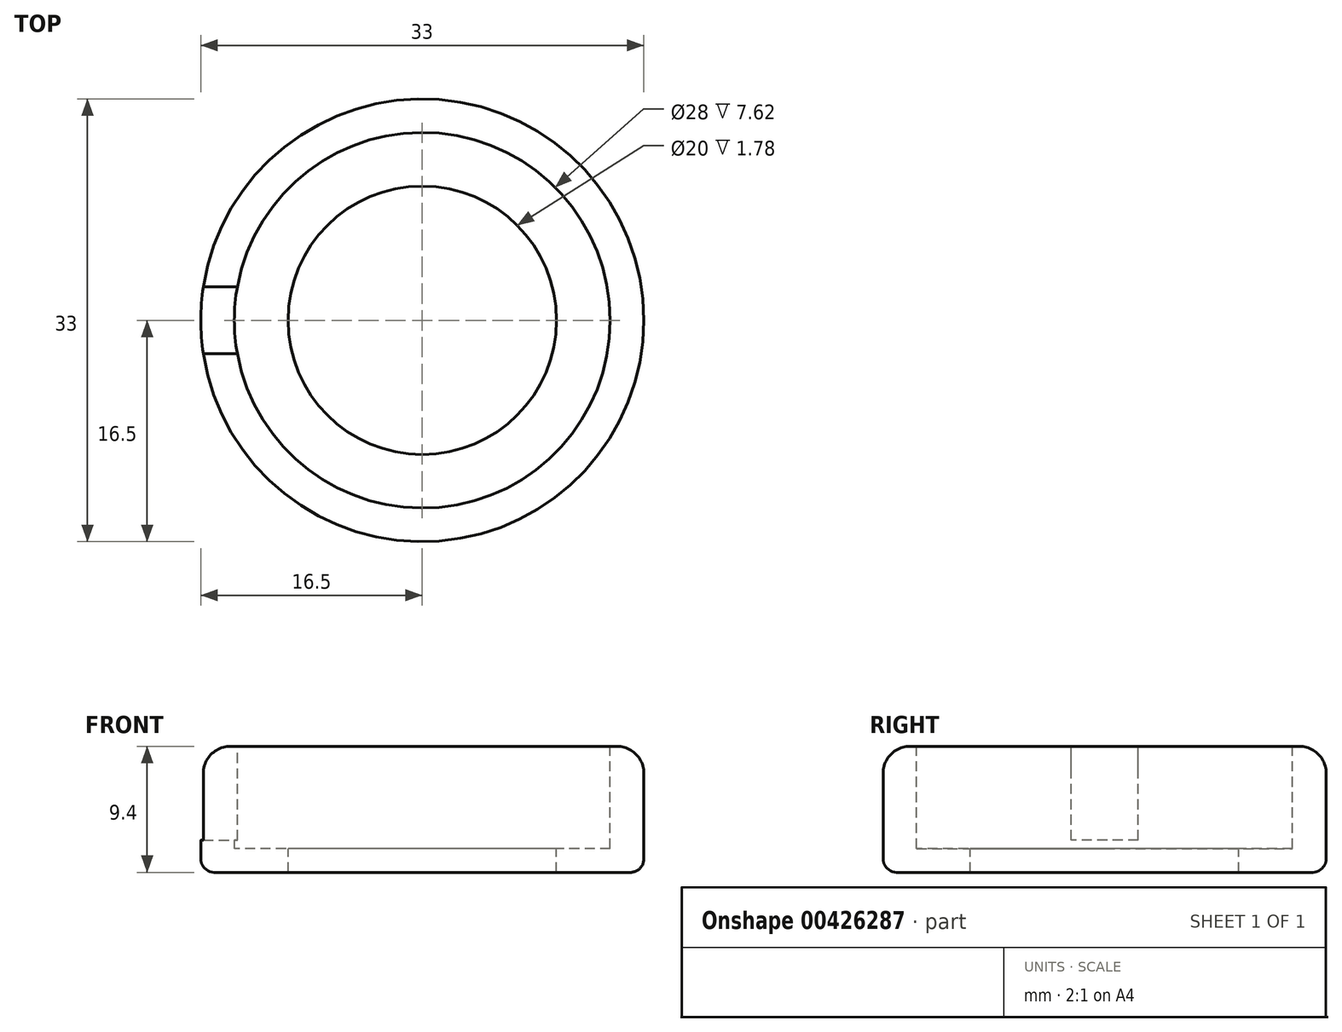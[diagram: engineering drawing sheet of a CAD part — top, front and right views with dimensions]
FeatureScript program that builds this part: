
annotation { "Feature Type Name" : "Feature", "Feature Type Description" : "" }
export const myFeature = defineFeature(function(context is Context, id is Id, definition is map)
    precondition{}
    {
        {
            var Q0;
            Q0=qCreatedBy(makeId("Top.planeOp"),FACE);
            var sketch = newSketch(context, id + "F0", { "sketchPlane" : qUnion([Q0])});
            skCircle(sketch, "E0", {"center": v(0, 0) * mm, "radius": 16.5 * mm});
            skSolve(sketch);
        }
        {
            var Q0;
            Q0 = qSketchRegion(id + "F0", true);
            extrude(context, id + "F1", {"entities" : qUnion([Q0]), "depth" : 9.4 * mm});
        }
        {
            var Q0;
            Q0=makeQuery(id+"F1.opExtrude","CAP_FACE",FACE,{"disambiguationData":[OSD([sQuery(id+"F0.wireOp",EDGE,"E0")])],"isStart":false});
            var sketch = newSketch(context, id + "F2", { "sketchPlane" : qUnion([Q0])});
            skCircle(sketch, "E1", {"center": v(0, 0) * mm, "radius": 14 * mm});
            skSolve(sketch);
        }
        {
            var Q0;
            Q0 = qSketchRegion(id + "F2", true);
            extrude(context, id + "F3", {"entities" : qUnion([Q0]), "operationType" : NewBodyOperationType.REMOVE, "oppositeDirection" : true, "depth" : 7.62 * mm});
        }
        {
            var Q0;
            Q0=makeQuery(id+"F1.opExtrude","CAP_EDGE",EDGE,{"disambiguationData":[OSD([sQuery(id+"F0.wireOp",EDGE,"E0")])],"isStart":false});
            fillet(context, id + "F4", {"entities" : qUnion([Q0]), "radius" : 2 * mm, "tangentPropagation" : true, "allowEdgeOverflow" : false});
        }
        {
            var Q0;
            Q0=makeQuery(id+"F1.opExtrude","CAP_FACE",FACE,{"disambiguationData":[OSD([sQuery(id+"F0.wireOp",EDGE,"E0")])],"isStart":false});
            var sketch = newSketch(context, id + "F5", { "sketchPlane" : qUnion([Q0])});
            skArc(sketch, "E2.0", {"start": v(-13.77, 2.5) * mm, "mid": v(-14, 0) * mm, "end": v(-13.77, -2.5) * mm});
            skArc(sketch, "E3.0", {"start": v(-16.3, 2.5) * mm, "mid": v(-16.5, 0) * mm, "end": v(-16.3, -2.5) * mm});
            skLineSegment(sketch, "E4", {"start": v(-14, 0) * mm, "end": v(-16.5, 0) * mm, "construction": true});
            skLineSegment(sketch, "E5", {"start": v(-16.3, 2.5) * mm, "end": v(-13.77, 2.5) * mm});
            skLineSegment(sketch, "E6.MirrorCS", {"start": v(-16.3, -2.5) * mm, "end": v(-13.77, -2.5) * mm});
            skSolve(sketch);
        }
        {
            var Q0;
            Q0 = qSketchRegion(id + "F5", true);
            extrude(context, id + "F6", {"entities" : qUnion([Q0]), "operationType" : NewBodyOperationType.REMOVE, "oppositeDirection" : true, "depth" : 7 * mm});
        }
        {
            var Q0;
            Q0=makeQuery(id+"F1.opExtrude","CAP_FACE",FACE,{"disambiguationData":[OSD([sQuery(id+"F0.wireOp",EDGE,"E0")])],"isStart":false});
            var sketch = newSketch(context, id + "F7", { "sketchPlane" : qUnion([Q0])});
            skArc(sketch, "E7.1", {"start": v(-13.91, 1.55) * mm, "mid": v(-14, 0) * mm, "end": v(-13.91, -1.55) * mm});
            skArc(sketch, "E8.0", {"start": v(-16.43, 1.55) * mm, "mid": v(-16.5, 0) * mm, "end": v(-16.43, -1.55) * mm});
            skLineSegment(sketch, "E9", {"start": v(-16.43, 1.55) * mm, "end": v(-13.91, 1.55) * mm});
            skPoint(sketch, "E10.orphan", {"position": v(-13.77, 2.5) * mm});
            skLineSegment(sketch, "E11.MirrorCS", {"start": v(-16.43, -1.55) * mm, "end": v(-13.91, -1.55) * mm});
            skPoint(sketch, "E12.orphan", {"position": v(-13.77, -2.5) * mm});
            skSolve(sketch);
        }
        {
            var Q0;
            Q0 = qSketchRegion(id + "F7", true);
            extrude(context, id + "F8", {"entities" : qUnion([Q0]), "operationType" : NewBodyOperationType.REMOVE, "oppositeDirection" : true, "depth" : 5.5 * mm});
        }
        {
            var Q0;
            Q0=makeQuery(id+"F1.opExtrude","CAP_EDGE",EDGE,{"disambiguationData":[OSD([sQuery(id+"F0.wireOp",EDGE,"E0")])],"isStart":true});
            fillet(context, id + "F9", {"entities" : qUnion([Q0]), "radius" : 1 * mm, "tangentPropagation" : true, "allowEdgeOverflow" : false});
        }
        {
            var Q0;
            Q0=makeQuery(id+"F3.boolean.opBoolean","COPY",FACE,{"derivedFrom":makeQuery(id+"F3.opExtrude","CAP_FACE",FACE,{"disambiguationData":[OSD([sQuery(id+"F2.wireOp",EDGE,"E1")])],"isStart":false})});
            var sketch = newSketch(context, id + "F10", { "sketchPlane" : qUnion([Q0])});
            skCircle(sketch, "E13", {"center": v(0, 0) * mm, "radius": 10 * mm});
            skSolve(sketch);
        }
        {
            var Q0;
            Q0 = qSketchRegion(id + "F10", true);
            extrude(context, id + "F11", {"entities" : qUnion([Q0]), "operationType" : NewBodyOperationType.REMOVE, "oppositeDirection" : true, "depth" : 3 * mm});
        }
    });
